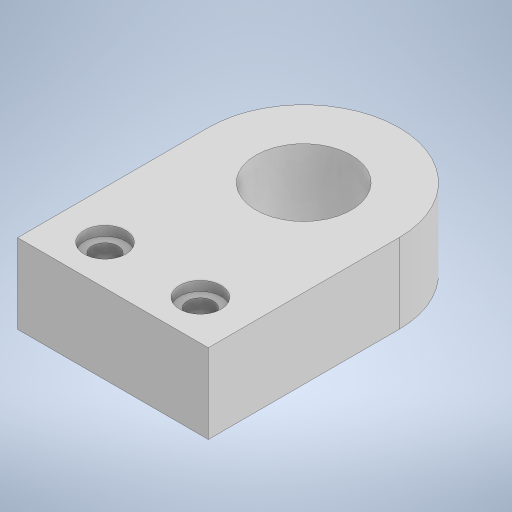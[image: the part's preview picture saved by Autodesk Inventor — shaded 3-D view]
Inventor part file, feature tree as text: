
AUTODESK INVENTOR PART (.ipt)
format: ipt  version: 2023.2 (Build 272271030, 271C)  size: 241,664 bytes
history: native  units: mm
features: extrude x3, sketch x3, projected_geometry x2
ambient origin geometry x8: Origin, YZ Plane, XZ Plane, XY Plane, X Axis, Y Axis, Z Axis, Center Point
bodies: Solid1 (feature_tree)
feature tree (8):
  extrude  "Extrusion1"  Depth=60.0mm
  extrude  "Extrusion2"  Depth=25.0mm TaperAngle=0.0deg
  extrude  "Extrusion3"  Depth=3.0mm
  sketch  "Sketch1"  dims[d0=60.0mm d1=60.0mm]
  sketch  "Sketch2"  dims[d2=30.0mm d3=25.0mm d4=0.0mm]
  projected_geometry  "Projected Loop1"
  sketch  "Sketch3"  dims[d5=65.0mm d6=8.1mm d7=30.0mm d8=0.0mm d9=0.0mm d10=13.1mm d11=13.1mm d12=3.0mm d13=0.0mm]
  projected_geometry  "Projected Loop2"
